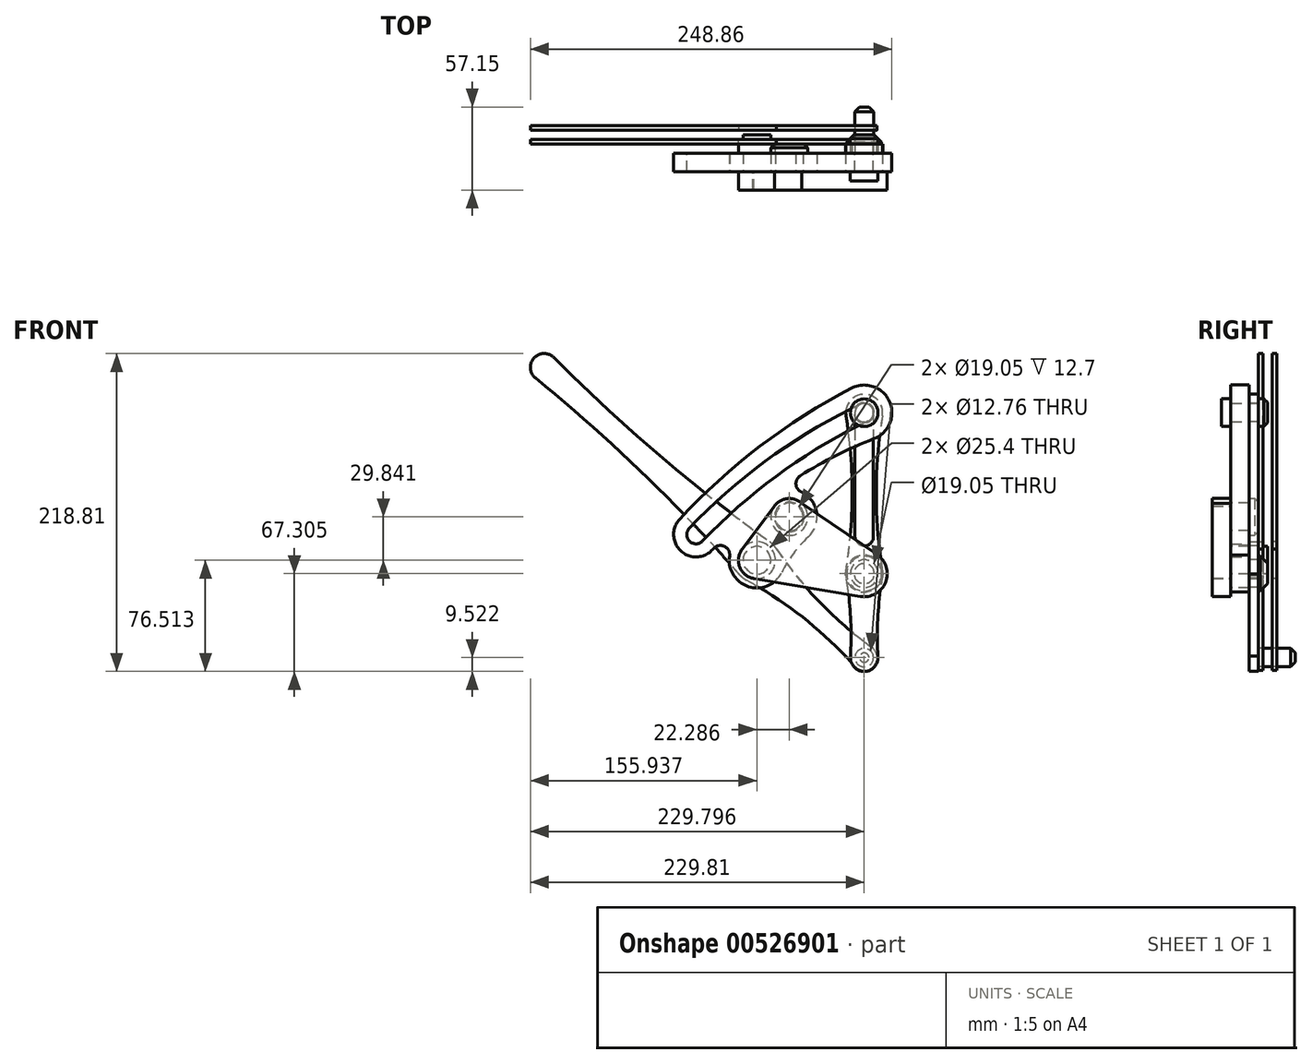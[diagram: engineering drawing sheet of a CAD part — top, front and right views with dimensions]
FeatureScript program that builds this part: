
annotation { "Feature Type Name" : "Feature", "Feature Type Description" : "" }
export const myFeature = defineFeature(function(context is Context, id is Id, definition is map)
    precondition{}
    {
        {
            var Q0;
            Q0=qCreatedBy(makeId("Front.planeOp"),FACE);
            var sketch = newSketch(context, id + "F0", { "sketchPlane" : qUnion([Q0])});
            skArc(sketch, "E0", {"start": v(6.86, -17.77) * mm, "mid": v(17.37, 7.83) * mm, "end": v(-8.77, 16.91) * mm});
            skArc(sketch, "E1", {"start": v(-8.77, 16.91) * mm, "mid": v(-71.88, -23.11) * mm, "end": v(-127.12, -73.44) * mm});
            skArc(sketch, "E2", {"start": v(-127.12, -73.44) * mm, "mid": v(-126.2, -95.24) * mm, "end": v(-104.4, -94.2) * mm});
            skArc(sketch, "E3", {"start": v(6.86, -17.77) * mm, "mid": v(-53.25, -49.46) * mm, "end": v(-104.4, -94.2) * mm});
            skArc(sketch, "E4.0.startCap", {"start": v(-2.72, 5.74) * mm, "mid": v(5.74, 2.72) * mm, "end": v(2.72, -5.74) * mm});
            skArc(sketch, "E4.0.endCap", {"start": v(-111.2, -88.25) * mm, "mid": v(-120.18, -88.48) * mm, "end": v(-120.41, -79.5) * mm});
            skArc(sketch, "E4.0.left", {"start": v(2.72, -5.74) * mm, "mid": v(-58.05, -41.74) * mm, "end": v(-111.2, -88.25) * mm});
            skArc(sketch, "E4.0.right", {"start": v(-2.72, 5.74) * mm, "mid": v(-65.5, -31.46) * mm, "end": v(-120.41, -79.5) * mm});
            skSolve(sketch);
        }
        {
            var Q0;
            Q0 = qSketchRegion(id + "F0", true);
            extrude(context, id + "F1", {"entities" : qUnion([Q0]), "depth" : 12.7 * mm, "offsetDistance" : 25.4 * mm});
        }
        {
            var Q0;
            Q0=makeQuery(id+"F1.opExtrude","CAP_FACE",FACE,{"disambiguationData":[OSD([sQuery(id+"F0.wireOp",EDGE,"E0"),sQuery(id+"F0.wireOp",EDGE,"E1"),sQuery(id+"F0.wireOp",EDGE,"E2"),sQuery(id+"F0.wireOp",EDGE,"E3"),sQuery(id+"F0.wireOp",EDGE,"E4.0.startCap"),sQuery(id+"F0.wireOp",EDGE,"E4.0.endCap"),sQuery(id+"F0.wireOp",EDGE,"E4.0.left"),sQuery(id+"F0.wireOp",EDGE,"E4.0.right")])],"isStart":false});
            var sketch = newSketch(context, id + "F2", { "sketchPlane" : qUnion([Q0])});
            skArc(sketch, "E5", {"start": v(-92.7, -98.65) * mm, "mid": v(-79.63, -119.7) * mm, "end": v(-56.82, -110.03) * mm});
            skPoint(sketch, "E5.first.point", {"position": v(-94.92, -84.22) * mm});
            skPoint(sketch, "E5.second.point", {"position": v(-56.82, -110.03) * mm});
            skPoint(sketch, "E5.third.point", {"position": v(-63.84, -85.36) * mm});
            skArc(sketch, "E6", {"start": v(-38.61, -85.65) * mm, "mid": v(-32.76, -68.81) * mm, "end": v(-43.4, -54.5) * mm});
            skPoint(sketch, "E6.first.point", {"position": v(-63.39, -56.75) * mm});
            skPoint(sketch, "E6.second.point", {"position": v(-38.61, -85.65) * mm});
            skPoint(sketch, "E6.third.point", {"position": v(-38.61, -85.65) * mm});
            skArc(sketch, "E7", {"start": v(-38.61, -85.65) * mm, "mid": v(-48.81, -97.02) * mm, "end": v(-56.82, -110.03) * mm});
            skCircle(sketch, "E8", {"center": v(-51.59, -71.7) * mm, "radius": 9.53 * mm});
            skCircle(sketch, "E9", {"center": v(-73.87, -101.55) * mm, "radius": 9.53 * mm});
            skArc(sketch, "E10.0", {"start": v(6.86, -17.77) * mm, "mid": v(-19.23, -29.34) * mm, "end": v(-44.07, -43.4) * mm});
            skPoint(sketch, "E11.newPointA", {"position": v(-104.4, -94.2) * mm});
            skArc(sketch, "E11.filletArc", {"start": v(-44.07, -43.4) * mm, "mid": v(-47.01, -49.15) * mm, "end": v(-43.4, -54.5) * mm});
            skArc(sketch, "E12.0", {"start": v(-127.12, -73.44) * mm, "mid": v(-126.2, -95.24) * mm, "end": v(-104.4, -94.2) * mm});
            skArc(sketch, "E13.0", {"start": v(-103.67, -93.4) * mm, "mid": v(-104.03, -93.8) * mm, "end": v(-104.4, -94.2) * mm});
            skArc(sketch, "E14.filletArc", {"start": v(-92.7, -98.65) * mm, "mid": v(-96.24, -91.96) * mm, "end": v(-103.67, -93.4) * mm});
            skSolve(sketch);
        }
        {
            var Q0;
            Q0=makeQuery(id+"F2.imprint","IMPRINT",FACE,{"disambiguationData":[TD([[makeQuery(id+"F2.imprint","IMPRINT",EDGE,{"derivedFrom":sQuery(id+"F2.wireOp",EDGE,"E5")}),1.0]])]});
            extrude(context, id + "F3", {"entities" : qUnion([Q0]), "operationType" : NewBodyOperationType.ADD, "oppositeDirection" : true, "depth" : 12.7 * mm, "offsetDistance" : 25.4 * mm});
        }
        {
            var Q0;
            Q0=qCreatedBy(makeId("Front.planeOp"),FACE);
            var sketch = newSketch(context, id + "F4", { "sketchPlane" : qUnion([Q0])});
            skArc(sketch, "E15", {"start": v(12.54, -2.01) * mm, "mid": v(0, 12.7) * mm, "end": v(-12.54, -2.01) * mm});
            skArc(sketch, "E16", {"start": v(-12.66, -109.56) * mm, "mid": v(-12.68, -111.65) * mm, "end": v(-12.36, -113.72) * mm});
            skArc(sketch, "E17", {"start": v(-9.48, -167.64) * mm, "mid": v(0, -178.06) * mm, "end": v(9.48, -167.64) * mm});
            skArc(sketch, "E18.trimOffspring", {"start": v(9.48, -167.64) * mm, "mid": v(9.48, -168.5) * mm, "end": v(9.49, -169.37) * mm});
            skPoint(sketch, "E19.start.orphan", {"position": v(12.87, 0) * mm});
            skArc(sketch, "E20", {"start": v(12.87, 0) * mm, "mid": v(8.28, -55.42) * mm, "end": v(12.87, -110.84) * mm});
            skArc(sketch, "E21.MirrorCS", {"start": v(-12.87, 0) * mm, "mid": v(-8.28, -55.42) * mm, "end": v(-12.87, -110.84) * mm});
            skArc(sketch, "E22", {"start": v(12.87, -110.84) * mm, "mid": v(9.46, -139.14) * mm, "end": v(9.48, -167.64) * mm});
            skArc(sketch, "E23.MirrorCS", {"start": v(-12.87, -110.84) * mm, "mid": v(-9.46, -139.14) * mm, "end": v(-9.48, -167.64) * mm});
            skCircle(sketch, "E24", {"center": v(-0.01, -110.76) * mm, "radius": 9.53 * mm});
            skArc(sketch, "E25.trimOffspring", {"start": v(12.5, -112.92) * mm, "mid": v(12.69, -110.83) * mm, "end": v(12.53, -108.74) * mm});
            skArc(sketch, "E26.0.startCap", {"start": v(-6.35, 0) * mm, "mid": v(0, 6.35) * mm, "end": v(6.35, 0) * mm});
            skArc(sketch, "E26.0.endCap", {"start": v(6.34, -85.26) * mm, "mid": v(-0.02, -91.6) * mm, "end": v(-6.36, -85.25) * mm});
            skLineSegment(sketch, "E26.0.left", {"start": v(6.35, 0) * mm, "end": v(6.34, -85.26) * mm});
            skLineSegment(sketch, "E26.0.right", {"start": v(-6.35, 0) * mm, "end": v(-6.36, -85.25) * mm});
            skSolve(sketch);
        }
        {
            var Q0;
            Q0 = qSketchRegion(id + "F4", true);
            extrude(context, id + "F5", {"entities" : qUnion([Q0]), "operationType" : NewBodyOperationType.ADD, "oppositeDirection" : true, "depth" : 6.35 * mm, "offsetDistance" : 25.4 * mm});
        }
        {
            var Q0;
            {var subQ2=sQuery(id+"F0.wireOp",EDGE,"E4.0.startCap");var subQ3=sQuery(id+"F4.wireOp",EDGE,"E15");var subQ5=sQuery(id+"F4.wireOp",EDGE,"E21.MirrorCS");Q0=makeQuery(id+"F5.boolean.opBoolean","SPLIT",FACE,{"disambiguationData":[TD([makeQuery(id+"F1.opExtrude","SWEPT_FACE",FACE,{"disambiguationData":[OSD([subQ2])]})])],"derivedFrom":makeQuery(id+"F5.opExtrude","CAP_FACE",FACE,{"disambiguationData":[OSD([subQ3,sQuery(id+"F4.wireOp",EDGE,"E16"),sQuery(id+"F4.wireOp",EDGE,"E17"),sQuery(id+"F4.wireOp",EDGE,"E20"),subQ5,sQuery(id+"F4.wireOp",EDGE,"E22"),sQuery(id+"F4.wireOp",EDGE,"E23.MirrorCS"),sQuery(id+"F4.wireOp",EDGE,"E24")])],"isStart":true})});}
            var sketch = newSketch(context, id + "F6", { "sketchPlane" : qUnion([Q0])});
            skCircle(sketch, "E27", {"center": v(0, 0) * mm, "radius": 6.35 * mm});
            skSolve(sketch);
        }
        {
            var Q0;
            Q0 = qSketchRegion(id + "F6", true);
            extrude(context, id + "F7", {"entities" : qUnion([Q0]), "depth" : 12.7 * mm, "offsetDistance" : 25.4 * mm});
        }
        {
            var Q0;
            Q0=makeQuery(id+"F7.opExtrude","CAP_FACE",FACE,{"disambiguationData":[OSD([sQuery(id+"F6.wireOp",EDGE,"E27")])],"isStart":false});
            var sketch = newSketch(context, id + "F8", { "sketchPlane" : qUnion([Q0])});
            skCircle(sketch, "E28", {"center": v(0, 0) * mm, "radius": 9.53 * mm});
            skSolve(sketch);
        }
        {
            var Q0;
            Q0 = qSketchRegion(id + "F8", true);
            extrude(context, id + "F9", {"entities" : qUnion([Q0]), "depth" : 6.35 * mm, "offsetDistance" : 25.4 * mm});
        }
        {
            var Q0;
            {var subQ0=sQuery(id+"F0.wireOp",EDGE,"E3");Q0=makeQuery(id+"F3.boolean.opBoolean","MERGE",FACE,{"derivedFrom":[makeQuery(id+"F1.opExtrude","CAP_FACE",FACE,{"disambiguationData":[OSD([sQuery(id+"F0.wireOp",EDGE,"E0"),sQuery(id+"F0.wireOp",EDGE,"E1"),sQuery(id+"F0.wireOp",EDGE,"E2"),subQ0,sQuery(id+"F0.wireOp",EDGE,"E4.0.startCap"),sQuery(id+"F0.wireOp",EDGE,"E4.0.endCap"),sQuery(id+"F0.wireOp",EDGE,"E4.0.left"),sQuery(id+"F0.wireOp",EDGE,"E4.0.right")])],"isStart":false}),makeQuery(id+"F3.opExtrude","CAP_FACE",FACE,{"disambiguationData":[OSD([subQ0,sQuery(id+"F2.wireOp",EDGE,"E5"),sQuery(id+"F2.wireOp",EDGE,"E6"),sQuery(id+"F2.wireOp",EDGE,"E7"),sQuery(id+"F2.wireOp",EDGE,"E8"),sQuery(id+"F2.wireOp",EDGE,"E9"),sQuery(id+"F2.wireOp",EDGE,"E11.filletArc"),sQuery(id+"F2.wireOp",EDGE,"E14.filletArc")])],"isStart":true})]});}
            var sketch = newSketch(context, id + "F10", { "sketchPlane" : qUnion([Q0])});
            skArc(sketch, "E29", {"start": v(-43.04, -62.31) * mm, "mid": v(-52.88, -59.07) * mm, "end": v(-61.86, -64.23) * mm});
            skArc(sketch, "E30", {"start": v(-84.05, -93.95) * mm, "mid": v(-85.8, -105.89) * mm, "end": v(-76.78, -113.9) * mm});
            skArc(sketch, "E31", {"start": v(-2.65, -126.41) * mm, "mid": v(14.72, -116.67) * mm, "end": v(8.91, -97.63) * mm});
            skLineSegment(sketch, "E32", {"start": v(-43.04, -62.31) * mm, "end": v(8.91, -97.63) * mm});
            skLineSegment(sketch, "E33", {"start": v(-61.86, -64.23) * mm, "end": v(-84.05, -93.95) * mm});
            skLineSegment(sketch, "E34", {"start": v(-76.78, -113.9) * mm, "end": v(-75.98, -114.07) * mm});
            skPoint(sketch, "E34.startSnap0", {"position": v(-79.63, -119.7) * mm});
            skPoint(sketch, "E35.orphan", {"position": v(-79.63, -113.33) * mm});
            skPoint(sketch, "E36.trimOffspring.end.orphan", {"position": v(0, -126.63) * mm});
            skLineSegment(sketch, "E37", {"start": v(-2.65, -126.41) * mm, "end": v(-75.98, -114.07) * mm});
            skSolve(sketch);
        }
        {
            var Q0;
            Q0 = qSketchRegion(id + "F10", true);
            extrude(context, id + "F11", {"entities" : qUnion([Q0]), "operationType" : NewBodyOperationType.ADD, "depth" : 12.7 * mm, "offsetDistance" : 25.4 * mm});
        }
        {
            var Q0;
            {var subQ2=sQuery(id+"F2.wireOp",EDGE,"E5");var subQ4=sQuery(id+"F10.wireOp",EDGE,"E31");var subQ5=sQuery(id+"F10.wireOp",EDGE,"E32");var subQ6=sQuery(id+"F10.wireOp",EDGE,"E37");Q0=makeQuery(id+"F11.boolean.opBoolean","SPLIT",FACE,{"disambiguationData":[TD([makeQuery(id+"F3.opExtrude","SWEPT_FACE",FACE,{"disambiguationData":[OSD([subQ2])]})])],"derivedFrom":makeQuery(id+"F11.opExtrude","CAP_FACE",FACE,{"disambiguationData":[OSD([sQuery(id+"F10.wireOp",EDGE,"E29"),sQuery(id+"F10.wireOp",EDGE,"E30"),subQ4,subQ5,sQuery(id+"F10.wireOp",EDGE,"E33"),sQuery(id+"F10.wireOp",EDGE,"E34"),subQ6])],"isStart":true})});}
            var sketch = newSketch(context, id + "F12", { "sketchPlane" : qUnion([Q0])});
            skCircle(sketch, "E38", {"center": v(0.01, -110.76) * mm, "radius": 12.7 * mm});
            skCircle(sketch, "E39", {"center": v(73.87, -101.55) * mm, "radius": 9.53 * mm});
            skCircle(sketch, "E40", {"center": v(51.59, -71.7) * mm, "radius": 9.53 * mm});
            skSolve(sketch);
        }
        {
            var Q0;
            Q0 = qSketchRegion(id + "F12", true);
            extrude(context, id + "F13", {"entities" : qUnion([Q0]), "depth" : 12.7 * mm, "offsetDistance" : 25.4 * mm});
        }
        {
            var Q0;
            Q0=makeQuery(id+"F13.opExtrude","CAP_FACE",FACE,{"disambiguationData":[OSD([sQuery(id+"F12.wireOp",EDGE,"E38")])],"isStart":false});
            var sketch = newSketch(context, id + "F14", { "sketchPlane" : qUnion([Q0])});
            skCircle(sketch, "E41", {"center": v(0.01, -110.76) * mm, "radius": 9.53 * mm});
            skSolve(sketch);
        }
        {
            var Q0;
            Q0 = qSketchRegion(id + "F14", true);
            extrude(context, id + "F15", {"entities" : qUnion([Q0]), "depth" : 6.35 * mm, "offsetDistance" : 25.4 * mm});
        }
        {
            var Q0;
            Q0=makeQuery(id+"F15.opExtrude","CAP_FACE",FACE,{"disambiguationData":[OSD([sQuery(id+"F14.wireOp",EDGE,"E41")])],"isStart":false});
            var sketch = newSketch(context, id + "F16", { "sketchPlane" : qUnion([Q0])});
            skCircle(sketch, "E42", {"center": v(0.01, -110.76) * mm, "radius": 12.03 * mm});
            skCircle(sketch, "E43", {"center": v(51.59, -71.7) * mm, "radius": 12.7 * mm});
            skCircle(sketch, "E44", {"center": v(73.87, -101.55) * mm, "radius": 12.7 * mm});
            skSolve(sketch);
        }
        {
            var Q0;
            Q0=makeQuery(id+"F16.imprint","IMPRINT",FACE,{"disambiguationData":[TD([[makeQuery(id+"F16.imprint","IMPRINT",EDGE,{"derivedFrom":sQuery(id+"F16.wireOp",EDGE,"E42")}),1.0]])]});
            var Q1;
            Q1=makeQuery(id+"F16.imprint","IMPRINT",FACE,{"disambiguationData":[TD([[makeQuery(id+"F16.imprint","IMPRINT",EDGE,{"derivedFrom":makeQuery(id+"F15.opExtrude","CAP_EDGE",EDGE,{"disambiguationData":[OSD([sQuery(id+"F14.wireOp",EDGE,"E41")])],"isStart":false})}),1.0]])]});
            extrude(context, id + "F17", {"entities" : qUnion([Q0, Q1]), "depth" : 6.35 * mm, "offsetDistance" : 25.4 * mm});
        }
        {
            var Q0;
            Q0=makeQuery(id+"F16.imprint","IMPRINT",FACE,{"disambiguationData":[TD([[makeQuery(id+"F16.imprint","IMPRINT",EDGE,{"derivedFrom":sQuery(id+"F16.wireOp",EDGE,"E43")}),1.0]])]});
            var Q1;
            Q1=makeQuery(id+"F16.imprint","IMPRINT",FACE,{"disambiguationData":[TD([[makeQuery(id+"F16.imprint","IMPRINT",EDGE,{"derivedFrom":sQuery(id+"F16.wireOp",EDGE,"E44")}),1.0]])]});
            extrude(context, id + "F18", {"entities" : qUnion([Q0, Q1]), "oppositeDirection" : true, "depth" : 6.35 * mm, "offsetDistance" : 25.4 * mm});
        }
        {
            var Q0;
            Q0=makeQuery(id+"F7.opExtrude","CAP_FACE",FACE,{"disambiguationData":[OSD([sQuery(id+"F6.wireOp",EDGE,"E27")])],"isStart":true});
            extrude(context, id + "F19", {"entities" : qUnion([Q0]), "depth" : 6.35 * mm, "offsetDistance" : 25.4 * mm});
        }
        {
            var Q0;
            Q0=makeQuery(id+"F19.opExtrude","CAP_FACE",FACE,{"disambiguationData":[OSD([sQuery(id+"F6.wireOp",EDGE,"E27")])],"isStart":false});
            var sketch = newSketch(context, id + "F20", { "sketchPlane" : qUnion([Q0])});
            skCircle(sketch, "E45", {"center": v(0, 0) * mm, "radius": 9.53 * mm});
            skSolve(sketch);
        }
        {
            var Q0;
            Q0 = qSketchRegion(id + "F20", true);
            extrude(context, id + "F21", {"entities" : qUnion([Q0]), "depth" : 6.35 * mm, "offsetDistance" : 25.4 * mm});
        }
        {
            var Q0;
            Q0=makeQuery(id+"F5.opExtrude","CAP_FACE",FACE,{"disambiguationData":[OSD([sQuery(id+"F4.wireOp",EDGE,"E15"),sQuery(id+"F4.wireOp",EDGE,"E16"),sQuery(id+"F4.wireOp",EDGE,"E17"),sQuery(id+"F4.wireOp",EDGE,"E20"),sQuery(id+"F4.wireOp",EDGE,"E21.MirrorCS"),sQuery(id+"F4.wireOp",EDGE,"E22"),sQuery(id+"F4.wireOp",EDGE,"E23.MirrorCS"),sQuery(id+"F4.wireOp",EDGE,"E24"),sQuery(id+"F4.wireOp",EDGE,"E26.0.startCap"),sQuery(id+"F4.wireOp",EDGE,"E26.0.endCap"),sQuery(id+"F4.wireOp",EDGE,"E26.0.left"),sQuery(id+"F4.wireOp",EDGE,"E26.0.right")])],"isStart":false});
            var sketch = newSketch(context, id + "F22", { "sketchPlane" : qUnion([Q0])});
            skCircle(sketch, "E46", {"center": v(0, -168.54) * mm, "radius": 6.38 * mm});
            skSolve(sketch);
        }
        {
            var Q0;
            Q0 = qSketchRegion(id + "F22", true);
            extrude(context, id + "F23", {"entities" : qUnion([Q0]), "operationType" : NewBodyOperationType.REMOVE, "oppositeDirection" : true, "depth" : 25.4 * mm, "offsetDistance" : 25.4 * mm});
        }
        {
            var Q0;
            Q0=makeQuery(id+"F5.opExtrude","CAP_FACE",FACE,{"disambiguationData":[OSD([sQuery(id+"F4.wireOp",EDGE,"E15"),sQuery(id+"F4.wireOp",EDGE,"E16"),sQuery(id+"F4.wireOp",EDGE,"E17"),sQuery(id+"F4.wireOp",EDGE,"E20"),sQuery(id+"F4.wireOp",EDGE,"E21.MirrorCS"),sQuery(id+"F4.wireOp",EDGE,"E22"),sQuery(id+"F4.wireOp",EDGE,"E23.MirrorCS"),sQuery(id+"F4.wireOp",EDGE,"E24"),sQuery(id+"F4.wireOp",EDGE,"E26.0.startCap"),sQuery(id+"F4.wireOp",EDGE,"E26.0.endCap"),sQuery(id+"F4.wireOp",EDGE,"E26.0.left"),sQuery(id+"F4.wireOp",EDGE,"E26.0.right")])],"isStart":false});
            var sketch = newSketch(context, id + "F24", { "sketchPlane" : qUnion([Q0])});
            skCircle(sketch, "E47", {"center": v(0, -168.54) * mm, "radius": 6.38 * mm});
            skSolve(sketch);
        }
        {
            var Q0;
            Q0 = qSketchRegion(id + "F24", true);
            extrude(context, id + "F25", {"entities" : qUnion([Q0]), "operationType" : NewBodyOperationType.ADD, "depth" : 25.4 * mm, "offsetDistance" : 25.4 * mm, "hasSecondDirection" : true, "secondDirectionOppositeDirection" : true, "secondDirectionDepth" : 6.35 * mm});
        }
        {
            var Q0;
            Q0=makeQuery(id+"F5.opExtrude","CAP_FACE",FACE,{"disambiguationData":[OSD([sQuery(id+"F4.wireOp",EDGE,"E15"),sQuery(id+"F4.wireOp",EDGE,"E16"),sQuery(id+"F4.wireOp",EDGE,"E17"),sQuery(id+"F4.wireOp",EDGE,"E20"),sQuery(id+"F4.wireOp",EDGE,"E21.MirrorCS"),sQuery(id+"F4.wireOp",EDGE,"E22"),sQuery(id+"F4.wireOp",EDGE,"E23.MirrorCS"),sQuery(id+"F4.wireOp",EDGE,"E24"),sQuery(id+"F4.wireOp",EDGE,"E26.0.startCap"),sQuery(id+"F4.wireOp",EDGE,"E26.0.endCap"),sQuery(id+"F4.wireOp",EDGE,"E26.0.left"),sQuery(id+"F4.wireOp",EDGE,"E26.0.right")])],"isStart":false});
            var sketch = newSketch(context, id + "F26", { "sketchPlane" : qUnion([Q0])});
            skArc(sketch, "E48.0", {"start": v(60.41, -93.85) * mm, "mid": v(30.58, -130.46) * mm, "end": v(-5.1, -161.4) * mm});
            skArc(sketch, "E48.1", {"start": v(81.37, -115.12) * mm, "mid": v(83.6, -113.63) * mm, "end": v(85.52, -111.78) * mm});
            skArc(sketch, "E48.2", {"start": v(81.37, -115.12) * mm, "mid": v(41.41, -141.5) * mm, "end": v(6.6, -174.34) * mm});
            skArc(sketch, "E48.3", {"start": v(-5.1, -161.4) * mm, "mid": v(-6.52, -174.43) * mm, "end": v(6.6, -174.34) * mm});
            skLineSegment(sketch, "E49", {"start": v(0, -168.54) * mm, "end": v(73.87, -101.55) * mm});
            skLineSegment(sketch, "E50", {"start": v(0, -168.54) * mm, "end": v(220.29, 31.23) * mm});
            skArc(sketch, "E51", {"start": v(226.3, 23.84) * mm, "mid": v(227.34, 37.62) * mm, "end": v(213.52, 37.93) * mm});
            skArc(sketch, "E52", {"start": v(64.83, -88.95) * mm, "mid": v(141.83, -28.62) * mm, "end": v(213.52, 37.93) * mm});
            skArc(sketch, "E53.MirrorCS", {"start": v(85.52, -111.78) * mm, "mid": v(153.08, -41.03) * mm, "end": v(226.3, 23.84) * mm});
            skArc(sketch, "E54.trimOffspring", {"start": v(64.83, -88.95) * mm, "mid": v(62.36, -91.17) * mm, "end": v(60.41, -93.85) * mm});
            skSolve(sketch);
        }
        {
            var Q0;
            {var subQ7=sQuery(id+"F26.wireOp",EDGE,"E48.1");Q0=makeQuery(id+"F26.imprint","IMPRINT",FACE,{"disambiguationData":[TD([[makeQuery(id+"F26.imprint","IMPRINT",EDGE,{"derivedFrom":subQ7}),1.0]])]});}
            var Q1;
            {var subQ0=sQuery(id+"F26.wireOp",EDGE,"E48.3");Q1=makeQuery(id+"F26.imprint","IMPRINT",FACE,{"disambiguationData":[TD([[makeQuery(id+"F26.imprint","IMPRINT",EDGE,{"derivedFrom":subQ0}),1.0]])]});}
            extrude(context, id + "F27", {"entities" : qUnion([Q0, Q1]), "depth" : 3.17 * mm, "offsetDistance" : 25.4 * mm});
        }
        {
            var Q0;
            Q0=makeQuery(id+"F27.opExtrude","CAP_FACE",FACE,{"disambiguationData":[OSD([sQuery(id+"F22.wireOp",EDGE,"E46"),sQuery(id+"F26.wireOp",EDGE,"E48.0"),sQuery(id+"F26.wireOp",EDGE,"E48.1"),sQuery(id+"F26.wireOp",EDGE,"E48.2"),sQuery(id+"F26.wireOp",EDGE,"E48.3")])],"isStart":false});
            var sketch = newSketch(context, id + "F28", { "sketchPlane" : qUnion([Q0])});
            skCircle(sketch, "E55", {"center": v(73.87, -101.55) * mm, "radius": 12.7 * mm});
            skSolve(sketch);
        }
        {
            var Q0;
            Q0=makeQuery(id+"F28.imprint","IMPRINT",FACE,{"disambiguationData":[TD([[makeQuery(id+"F28.imprint","IMPRINT",EDGE,{"derivedFrom":sQuery(id+"F28.wireOp",EDGE,"E55")}),1.0]])]});
            extrude(context, id + "F29", {"entities" : qUnion([Q0]), "oppositeDirection" : true, "depth" : 3.17 * mm, "offsetDistance" : 25.4 * mm});
        }
        {
            var Q0;
            Q0=makeQuery(id+"F29.opExtrude","CAP_FACE",FACE,{"disambiguationData":[OSD([sQuery(id+"F28.wireOp",EDGE,"E55")])],"isStart":true});
            var Q1;
            Q1=sQuery(id+"F16.wireOp",EDGE,"E44");
            extrude(context, id + "F30", {"entities" : qUnion([Q0]), "operationType" : NewBodyOperationType.REMOVE, "surfaceEntities" : qUnion([Q1]), "oppositeDirection" : true, "depth" : 3.17 * mm, "offsetDistance" : 25.4 * mm});
        }
        {
            var Q0;
            Q0=makeQuery(id+"F28.imprint","IMPRINT",FACE,{"disambiguationData":[TD([[makeQuery(id+"F28.imprint","IMPRINT",EDGE,{"derivedFrom":sQuery(id+"F28.wireOp",EDGE,"E55")}),-1.0]])]});
            var sketch = newSketch(context, id + "F31", { "sketchPlane" : qUnion([Q0])});
            skCircle(sketch, "E56.0", {"center": v(73.87, -101.55) * mm, "radius": 12.7 * mm});
            skCircle(sketch, "E57", {"center": v(73.87, -101.55) * mm, "radius": 9.53 * mm});
            skSolve(sketch);
        }
        {
            var Q0;
            Q0=makeQuery(id+"F31.imprint","IMPRINT",FACE,{"disambiguationData":[TD([[makeQuery(id+"F31.imprint","IMPRINT",EDGE,{"derivedFrom":sQuery(id+"F31.wireOp",EDGE,"E57")}),1.0]])]});
            extrude(context, id + "F32", {"entities" : qUnion([Q0]), "operationType" : NewBodyOperationType.ADD, "depth" : 3.17 * mm, "offsetDistance" : 25.4 * mm});
        }
        {
            var Q0;
            Q0=makeQuery(id+"F27.opExtrude","SWEPT_BODY",BODY,{"disambiguationData":[OSD([sQuery(id+"F22.wireOp",EDGE,"E46"),sQuery(id+"F26.wireOp",EDGE,"E48.0"),sQuery(id+"F26.wireOp",EDGE,"E48.1"),sQuery(id+"F26.wireOp",EDGE,"E48.2"),sQuery(id+"F26.wireOp",EDGE,"E48.3"),sQuery(id+"F26.wireOp",EDGE,"E51"),sQuery(id+"F26.wireOp",EDGE,"E52"),sQuery(id+"F26.wireOp",EDGE,"E53.MirrorCS"),sQuery(id+"F26.wireOp",EDGE,"E54.trimOffspring")])]});
            var Q1;
            Q1=makeQuery(id+"F32.opExtrude","CAP_FACE",FACE,{"disambiguationData":[OSD([sQuery(id+"F31.wireOp",EDGE,"E57")])],"isStart":false});
            mirror(context, id + "F33", {"entities" : qUnion([Q0]), "mirrorPlane" : qUnion([Q1])});
        }
        {
            var Q0;
            Q0=makeQuery(id+"F17.opExtrude","CAP_EDGE",EDGE,{"disambiguationData":[OSD([sQuery(id+"F16.wireOp",EDGE,"E42")])],"isStart":false});
            chamfer(context, id + "F34", {"entities" : qUnion([Q0]), "width" : 5.08 * mm, "tangentPropagation" : true});
        }
        {
            var Q0;
            Q0=makeQuery(id+"F21.opExtrude","CAP_EDGE",EDGE,{"disambiguationData":[OSD([sQuery(id+"F20.wireOp",EDGE,"E45")])],"isStart":false});
            chamfer(context, id + "F35", {"entities" : qUnion([Q0]), "width" : 2.54 * mm, "tangentPropagation" : true});
        }
        {
            var Q0;
            Q0=makeQuery(id+"F18.opExtrude","CAP_EDGE",EDGE,{"disambiguationData":[OSD([sQuery(id+"F16.wireOp",EDGE,"E43")])],"isStart":true});
            chamfer(context, id + "F36", {"entities" : qUnion([Q0]), "width" : 2.54 * mm, "tangentPropagation" : true});
        }
        {
            var Q0;
            Q0=makeQuery(id+"F25.opExtrude","CAP_EDGE",EDGE,{"disambiguationData":[OSD([sQuery(id+"F24.wireOp",EDGE,"E47")])],"isStart":false});
            chamfer(context, id + "F37", {"entities" : qUnion([Q0]), "width" : 3.17 * mm, "tangentPropagation" : true});
        }
    });
